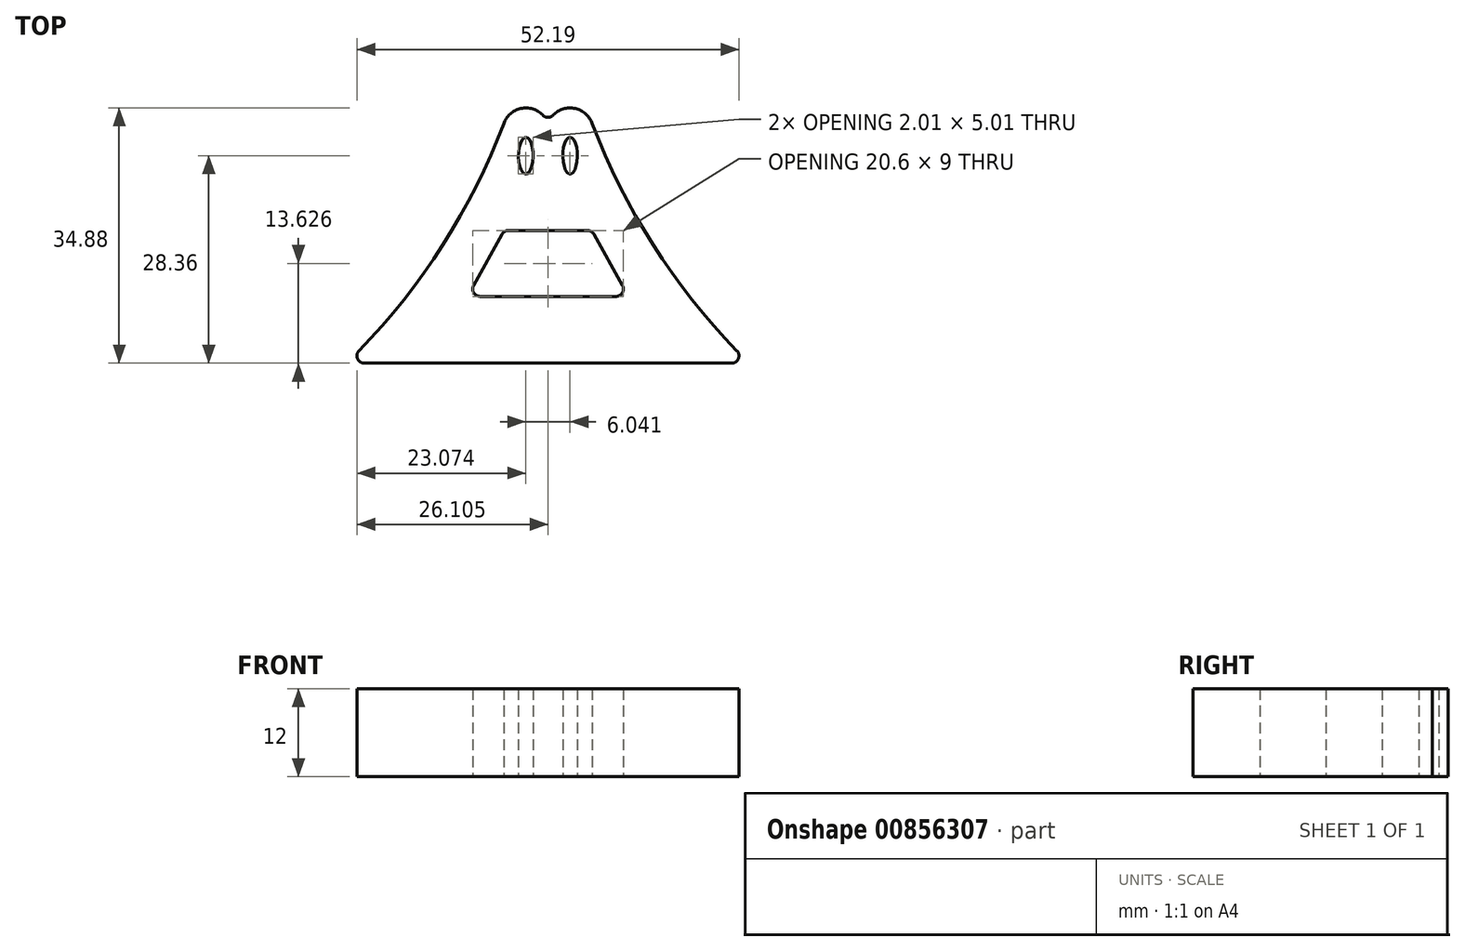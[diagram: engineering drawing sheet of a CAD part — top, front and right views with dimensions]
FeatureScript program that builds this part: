
annotation { "Feature Type Name" : "Feature", "Feature Type Description" : "" }
export const myFeature = defineFeature(function(context is Context, id is Id, definition is map)
    precondition{}
    {
        {
            var Q0;
            Q0=qCreatedBy(makeId("Top.planeOp"),FACE);
            var sketch = newSketch(context, id + "F0", { "sketchPlane" : qUnion([Q0])});
            skLineSegment(sketch, "E0", {"start": v(39.6, -59.33) * mm, "end": v(89.79, -59.33) * mm});
            skArc(sketch, "E1", {"start": v(38.88, -57.63) * mm, "mid": v(50.34, -43.13) * mm, "end": v(58.65, -26.63) * mm});
            skArc(sketch, "E2", {"start": v(70.74, -26.63) * mm, "mid": v(79.05, -43.13) * mm, "end": v(90.5, -57.63) * mm});
            skPoint(sketch, "E3.orphan", {"position": v(64.7, 6.06) * mm});
            skPoint(sketch, "E4.visualSharp", {"position": v(64.7, -26.63) * mm});
            skPoint(sketch, "E5.visualSharp", {"position": v(37.2, -59.33) * mm});
            skArc(sketch, "E5.filletArc", {"start": v(38.88, -57.63) * mm, "mid": v(38.68, -58.72) * mm, "end": v(39.6, -59.33) * mm});
            skPoint(sketch, "E6.visualSharp", {"position": v(92.2, -59.33) * mm});
            skArc(sketch, "E6.filletArc", {"start": v(89.79, -59.33) * mm, "mid": v(90.7, -58.72) * mm, "end": v(90.5, -57.63) * mm});
            skLineSegment(sketch, "E7", {"start": v(59.27, -41.2) * mm, "end": v(70.1, -41.2) * mm});
            skLineSegment(sketch, "E8", {"start": v(55.4, -50.2) * mm, "end": v(74, -50.2) * mm});
            skLineSegment(sketch, "E9", {"start": v(64.68, -41.2) * mm, "end": v(64.7, -50.2) * mm, "construction": true});
            skLineSegment(sketch, "E10", {"start": v(58.4, -41.72) * mm, "end": v(54.53, -48.72) * mm});
            skLineSegment(sketch, "E11", {"start": v(70.97, -41.72) * mm, "end": v(74.88, -48.72) * mm});
            skPoint(sketch, "E12.visualSharp", {"position": v(58.68, -41.2) * mm});
            skArc(sketch, "E12.filletArc", {"start": v(59.27, -41.2) * mm, "mid": v(58.76, -41.34) * mm, "end": v(58.4, -41.72) * mm});
            skPoint(sketch, "E13.visualSharp", {"position": v(70.68, -41.2) * mm});
            skArc(sketch, "E13.filletArc", {"start": v(70.97, -41.72) * mm, "mid": v(70.6, -41.34) * mm, "end": v(70.1, -41.2) * mm});
            skPoint(sketch, "E14.visualSharp", {"position": v(75.7, -50.2) * mm});
            skArc(sketch, "E14.filletArc", {"start": v(74, -50.2) * mm, "mid": v(74.87, -49.71) * mm, "end": v(74.88, -48.72) * mm});
            skPoint(sketch, "E15.visualSharp", {"position": v(53.7, -50.2) * mm});
            skArc(sketch, "E15.filletArc", {"start": v(54.53, -48.72) * mm, "mid": v(54.54, -49.71) * mm, "end": v(55.4, -50.2) * mm});
            skEllipse(sketch, "E16", {"center": v(61.67, -30.97) * mm, "majorRadius": 2.5 * mm, "minorRadius": 1 * mm, "majorAxis": v(0, 1)});
            skEllipse(sketch, "E17.MirrorC", {"center": v(67.72, -30.97) * mm, "majorRadius": 2.5 * mm, "minorRadius": 1 * mm, "majorAxis": v(0, 1)});
            skLineSegment(sketch, "E18", {"start": v(58.65, -26.63) * mm, "end": v(70.74, -26.63) * mm, "construction": true});
            skLineSegment(sketch, "E19", {"start": v(64.7, -26.63) * mm, "end": v(64.7, -59.33) * mm, "construction": true});
            skLineSegment(sketch, "E20", {"start": v(61.67, -28.47) * mm, "end": v(61.67, -24.47) * mm, "construction": true});
            skLineSegment(sketch, "E21.MirrorCS", {"start": v(67.72, -28.47) * mm, "end": v(67.72, -24.47) * mm, "construction": true});
            skArc(sketch, "E22", {"start": v(63.97, -25.43) * mm, "mid": v(60.97, -24.53) * mm, "end": v(58.65, -26.63) * mm});
            skArc(sketch, "E23", {"start": v(70.74, -26.63) * mm, "mid": v(68.41, -24.53) * mm, "end": v(65.42, -25.43) * mm});
            skArc(sketch, "E24.filletArc", {"start": v(63.97, -25.43) * mm, "mid": v(64.7, -25.74) * mm, "end": v(65.42, -25.43) * mm});
            skSolve(sketch);
        }
        {
            var Q0;
            Q0=makeQuery(id+"F0.imprint","IMPRINT",FACE,{"disambiguationData":[TD([[makeQuery(id+"F0.imprint","IMPRINT",EDGE,{"derivedFrom":sQuery(id+"F0.wireOp",EDGE,"E0")}),1.0]])]});
            extrude(context, id + "F1", {"entities" : qUnion([Q0]), "depth" : 12 * mm, "offsetDistance" : 25 * mm});
        }
    });
